annotation { "Feature Type Name" : "Feature", "Feature Type Description" : "" }
export const myFeature = defineFeature(function(context is Context, id is Id, definition is map)
    precondition{}
    {
        {
            assignVariable(context, id + "F0", {"name" : "SignDepth", "anyValue" : 1 / 8});
        }
        {
            var Q0;
            Q0=qCreatedBy(makeId("Front.planeOp"),FACE);
            var sketch = newSketch(context, id + "F1", { "sketchPlane" : qUnion([Q0])});
            skLineSegment(sketch, "E0.bottom", {"start": v(-106.06, 127) * mm, "end": v(0, 127) * mm});
            skLineSegment(sketch, "E0.top", {"start": v(-106.06, 0) * mm, "end": v(0, 0) * mm});
            skLineSegment(sketch, "E0.left", {"start": v(-106.06, 127) * mm, "end": v(-106.06, 0) * mm});
            skLineSegment(sketch, "E0.right", {"start": v(0, 127) * mm, "end": v(0, 0) * mm});
            skLineSegment(sketch, "E1.bottom", {"start": v(-105.6, 126.55) * mm, "end": v(-0.45, 126.55) * mm});
            skLineSegment(sketch, "E1.top", {"start": v(-105.6, 0.45) * mm, "end": v(-0.45, 0.45) * mm});
            skLineSegment(sketch, "E1.left", {"start": v(-105.6, 126.55) * mm, "end": v(-105.6, 0.45) * mm});
            skLineSegment(sketch, "E1.right", {"start": v(-0.45, 126.55) * mm, "end": v(-0.45, 0.45) * mm});
            skSolve(sketch);
        }
        {
            var Q0;
            Q0 = qSketchRegion(id + "F1", true);
            extrude(context, id + "F2", {"entities" : qUnion([Q0]), "depth" : (getVariable(context, 'SignDepth')) * mm, "offsetDistance" : 25.4 * mm});
        }
        {
            var Q0;
            Q0=qCreatedBy(makeId("Front.planeOp"),FACE);
            var sketch = newSketch(context, id + "F3", { "sketchPlane" : qUnion([Q0])});
            skLineSegment(sketch, "E2.bottom", {"start": v(-105.6, 126.55) * mm, "end": v(-0.45, 126.55) * mm});
            skLineSegment(sketch, "E2.top", {"start": v(-105.6, 0.45) * mm, "end": v(-0.45, 0.45) * mm});
            skLineSegment(sketch, "E2.left", {"start": v(-105.6, 126.55) * mm, "end": v(-105.6, 0.45) * mm});
            skLineSegment(sketch, "E2.right", {"start": v(-0.45, 126.55) * mm, "end": v(-0.45, 0.45) * mm});
            skSolve(sketch);
        }
        {
            var Q0;
            Q0 = qSketchRegion(id + "F3", true);
            extrude(context, id + "F4", {"entities" : qUnion([Q0]), "depth" : (getVariable(context, 'SignDepth')) * mm, "offsetDistance" : 25.4 * mm});
        }
        {
            var Q0;
            Q0=makeQuery(id+"F4.opExtrude","CAP_FACE",FACE,{"disambiguationData":[OSD([sQuery(id+"F3.wireOp",EDGE,"E2.bottom"),sQuery(id+"F3.wireOp",EDGE,"E2.top"),sQuery(id+"F3.wireOp",EDGE,"E2.left"),sQuery(id+"F3.wireOp",EDGE,"E2.right")])],"isStart":false});
            var sketch = newSketch(context, id + "F5", { "sketchPlane" : qUnion([Q0])});
            skText(sketch, "E3", { "text": "POLICE TELEPHONE", "fontName": "RobotoSlab-Regular.ttf"});
            skText(sketch, "E4", { "text": "FREE", "fontName": "NotoSerif-Bold.ttf"});
            skText(sketch, "E5", { "text": "FOR USE OF", "fontName": "NotoSerif-Regular.ttf"});
            skText(sketch, "E6", { "text": "PUBLIC", "fontName": "NotoSerif-Bold.ttf"});
            skText(sketch, "E7", { "text": "ADVICE & ASSISTANCE\n", "fontName": "NotoSans-Regular.ttf"});
            skText(sketch, "E8", { "text": "OBTAINABLE IMMEDIATELY", "fontName": "OpenSans-Regular.ttf"});
            skText(sketch, "E9", { "text": "OFFICER & CARS", "fontName": "OpenSans-Regular.ttf"});
            skText(sketch, "E10", { "text": "RESPOND TO ALL CALLS", "fontName": "OpenSans-Regular.ttf"});
            skText(sketch, "E11", { "text": "PULL TO OPEN", "fontName": "OpenSans-Regular.ttf"});
            const initialGuessF5  = {"E3": [-0.05014, 0.12437, 1, 0, 0.00018], "E4": [-0.05014, 0.12389, 1, 0, 0.00066], "E5": [-0.05014, 0.12424, 1, 0, 0.0003], "E6": [-0.05014, 0.12408, 1, 0, 0.00046], "E7": [-0.05014, 0.12438, 1, 0, 0.00017], "E8": [-0.07343, 0.0752, 1, 0, 0.00276], "E9": [-0.07343, 0.07332, 1, 0, 0.00465], "E10": [-0.07343, 0.07482, 1, 0, 0.00314], "E11": [-0.07343, 0.07283, 1, 0, 0.00513]};
            skSetInitialGuess(sketch, initialGuessF5);
            skSolve(sketch);
        }
        {
            var Q0;
            Q0 = qSketchRegion(id + "F5", true);
            extrude(context, id + "F6", {"entities" : qUnion([Q0]), "oppositeDirection" : true, "depth" : (getVariable(context, 'SignDepth') - (1 / 16)) * mm, "offsetDistance" : 25.4 * mm});
        }
        {
            var Q0;
            Q0=makeQuery(id+"F6.opExtrude","CAP_FACE",FACE,{"disambiguationData":[OSD([sQuery(id+"F5.wireOp",EDGE,"E4.sketch_text.stroke-32"),sQuery(id+"F5.wireOp",EDGE,"E4.sketch_text.stroke-33"),sQuery(id+"F5.wireOp",EDGE,"E4.sketch_text.stroke-34"),sQuery(id+"F5.wireOp",EDGE,"E4.sketch_text.stroke-35"),sQuery(id+"F5.wireOp",EDGE,"E4.sketch_text.stroke-36"),sQuery(id+"F5.wireOp",EDGE,"E4.sketch_text.stroke-37"),sQuery(id+"F5.wireOp",EDGE,"E4.sketch_text.stroke-38"),sQuery(id+"F5.wireOp",EDGE,"E4.sketch_text.stroke-39"),sQuery(id+"F5.wireOp",EDGE,"E4.sketch_text.stroke-40"),sQuery(id+"F5.wireOp",EDGE,"E4.sketch_text.stroke-41"),sQuery(id+"F5.wireOp",EDGE,"E4.sketch_text.stroke-42"),sQuery(id+"F5.wireOp",EDGE,"E4.sketch_text.stroke-43"),sQuery(id+"F5.wireOp",EDGE,"E4.sketch_text.stroke-44"),sQuery(id+"F5.wireOp",EDGE,"E4.sketch_text.stroke-45"),sQuery(id+"F5.wireOp",EDGE,"E4.sketch_text.stroke-46"),sQuery(id+"F5.wireOp",EDGE,"E4.sketch_text.stroke-47"),sQuery(id+"F5.wireOp",EDGE,"E4.sketch_text.stroke-48"),sQuery(id+"F5.wireOp",EDGE,"E4.sketch_text.stroke-49"),sQuery(id+"F5.wireOp",EDGE,"E4.sketch_text.stroke-50"),sQuery(id+"F5.wireOp",EDGE,"E4.sketch_text.stroke-51"),sQuery(id+"F5.wireOp",EDGE,"E4.sketch_text.stroke-52"),sQuery(id+"F5.wireOp",EDGE,"E4.sketch_text.stroke-53"),sQuery(id+"F5.wireOp",EDGE,"E4.sketch_text.stroke-54"),sQuery(id+"F5.wireOp",EDGE,"E4.sketch_text.stroke-55"),sQuery(id+"F5.wireOp",EDGE,"E4.sketch_text.stroke-56"),sQuery(id+"F5.wireOp",EDGE,"E4.sketch_text.stroke-57"),sQuery(id+"F5.wireOp",EDGE,"E4.sketch_text.stroke-58"),sQuery(id+"F5.wireOp",EDGE,"E4.sketch_text.stroke-59"),sQuery(id+"F5.wireOp",EDGE,"E4.sketch_text.stroke-60"),sQuery(id+"F5.wireOp",EDGE,"E4.sketch_text.stroke-61"),sQuery(id+"F5.wireOp",EDGE,"E4.sketch_text.stroke-62"),sQuery(id+"F5.wireOp",EDGE,"E4.sketch_text.stroke-63"),sQuery(id+"F5.wireOp",EDGE,"E4.sketch_text.stroke-64"),sQuery(id+"F5.wireOp",EDGE,"E4.sketch_text.stroke-65"),sQuery(id+"F5.wireOp",EDGE,"E4.sketch_text.stroke-66"),sQuery(id+"F5.wireOp",EDGE,"E4.sketch_text.stroke-67"),sQuery(id+"F5.wireOp",EDGE,"E4.sketch_text.stroke-68"),sQuery(id+"F5.wireOp",EDGE,"E4.sketch_text.stroke-69"),sQuery(id+"F5.wireOp",EDGE,"E4.sketch_text.stroke-70"),sQuery(id+"F5.wireOp",EDGE,"E4.sketch_text.stroke-71"),sQuery(id+"F5.wireOp",EDGE,"E4.sketch_text.stroke-72"),sQuery(id+"F5.wireOp",EDGE,"E4.sketch_text.stroke-73"),sQuery(id+"F5.wireOp",EDGE,"E4.sketch_text.stroke-74"),sQuery(id+"F5.wireOp",EDGE,"E4.sketch_text.stroke-75"),sQuery(id+"F5.wireOp",EDGE,"E4.sketch_text.stroke-76"),sQuery(id+"F5.wireOp",EDGE,"E4.sketch_text.stroke-77"),sQuery(id+"F5.wireOp",EDGE,"E4.sketch_text.stroke-78"),sQuery(id+"F5.wireOp",EDGE,"E4.sketch_text.stroke-79"),sQuery(id+"F5.wireOp",EDGE,"E4.sketch_text.stroke-80"),sQuery(id+"F5.wireOp",EDGE,"E4.sketch_text.stroke-81"),sQuery(id+"F5.wireOp",EDGE,"E4.sketch_text.stroke-82"),sQuery(id+"F5.wireOp",EDGE,"E4.sketch_text.stroke-83"),sQuery(id+"F5.wireOp",EDGE,"E4.sketch_text.stroke-84")])],"isStart":false});
            var sketch = newSketch(context, id + "F7", { "sketchPlane" : qUnion([Q0])});
            skLineSegment(sketch, "E12.bottom", {"start": v(8.45, 113.9) * mm, "end": v(98.1, 113.9) * mm});
            skLineSegment(sketch, "E12.top", {"start": v(8.45, 113.87) * mm, "end": v(53.25, 113.87) * mm});
            skLineSegment(sketch, "E12.left", {"start": v(8.45, 113.9) * mm, "end": v(8.45, 113.87) * mm});
            skLineSegment(sketch, "E12.right", {"start": v(98.1, 113.9) * mm, "end": v(98.1, 113.87) * mm});
            skLineSegment(sketch, "E13.bottom", {"start": v(38.19, 102.7) * mm, "end": v(53.25, 102.7) * mm});
            skLineSegment(sketch, "E13.top", {"start": v(38.19, 102.68) * mm, "end": v(53.25, 102.68) * mm});
            skLineSegment(sketch, "E13.left", {"start": v(38.19, 102.7) * mm, "end": v(38.19, 102.68) * mm});
            skLineSegment(sketch, "E13.right", {"start": v(68.48, 102.7) * mm, "end": v(68.48, 102.68) * mm});
            skLineSegment(sketch, "E14.bottom", {"start": v(27.21, 87.3) * mm, "end": v(53.25, 87.3) * mm});
            skLineSegment(sketch, "E14.top", {"start": v(27.21, 87.27) * mm, "end": v(53.25, 87.27) * mm});
            skLineSegment(sketch, "E14.left", {"start": v(27.21, 87.3) * mm, "end": v(27.21, 87.27) * mm});
            skLineSegment(sketch, "E14.right", {"start": v(78.88, 87.3) * mm, "end": v(78.88, 87.27) * mm});
            skLineSegment(sketch, "E15.bottom", {"start": v(33.5, 72.5) * mm, "end": v(53.25, 72.5) * mm});
            skLineSegment(sketch, "E15.top", {"start": v(33.5, 72.48) * mm, "end": v(49.48, 72.48) * mm});
            skLineSegment(sketch, "E15.left", {"start": v(33.5, 72.5) * mm, "end": v(33.5, 72.48) * mm});
            skLineSegment(sketch, "E15.right", {"start": v(77.3, 72.5) * mm, "end": v(77.3, 72.48) * mm});
            skLineSegment(sketch, "E16.bottom", {"start": v(16.99, 54.8) * mm, "end": v(49.48, 54.8) * mm});
            skLineSegment(sketch, "E16.top", {"start": v(16.99, 54.78) * mm, "end": v(49.48, 54.78) * mm});
            skLineSegment(sketch, "E16.left", {"start": v(16.99, 54.8) * mm, "end": v(16.99, 54.78) * mm});
            skLineSegment(sketch, "E16.right", {"start": v(88.68, 54.8) * mm, "end": v(88.68, 54.78) * mm});
            skLineSegment(sketch, "E17.bottom", {"start": v(10.24, 45.92) * mm, "end": v(49.48, 45.92) * mm});
            skLineSegment(sketch, "E17.top", {"start": v(10.24, 45.9) * mm, "end": v(49.48, 45.9) * mm});
            skLineSegment(sketch, "E17.left", {"start": v(10.24, 45.92) * mm, "end": v(10.24, 45.9) * mm});
            skLineSegment(sketch, "E17.right", {"start": v(97.52, 45.92) * mm, "end": v(97.52, 45.9) * mm});
            skLineSegment(sketch, "E18.bottom", {"start": v(29.77, 33.68) * mm, "end": v(49.48, 33.68) * mm});
            skLineSegment(sketch, "E18.top", {"start": v(29.77, 33.66) * mm, "end": v(49.48, 33.66) * mm});
            skLineSegment(sketch, "E18.left", {"start": v(29.77, 33.68) * mm, "end": v(29.77, 33.66) * mm});
            skLineSegment(sketch, "E18.right", {"start": v(76.3, 33.68) * mm, "end": v(76.3, 33.66) * mm});
            skLineSegment(sketch, "E19.bottom", {"start": v(19.2, 25.81) * mm, "end": v(49.48, 25.81) * mm});
            skLineSegment(sketch, "E19.top", {"start": v(19.2, 25.79) * mm, "end": v(49.48, 25.79) * mm});
            skLineSegment(sketch, "E19.left", {"start": v(19.2, 25.81) * mm, "end": v(19.2, 25.79) * mm});
            skLineSegment(sketch, "E19.right", {"start": v(86.92, 25.81) * mm, "end": v(86.92, 25.79) * mm});
            skLineSegment(sketch, "E20.bottom", {"start": v(10.07, 10.9) * mm, "end": v(49.48, 10.9) * mm});
            skLineSegment(sketch, "E20.top", {"start": v(10.07, 10.88) * mm, "end": v(95.56, 10.88) * mm});
            skLineSegment(sketch, "E20.left", {"start": v(10.07, 10.9) * mm, "end": v(10.07, 10.88) * mm});
            skLineSegment(sketch, "E20.right", {"start": v(95.56, 10.9) * mm, "end": v(95.56, 10.88) * mm});
            skLineSegment(sketch, "E21.left", {"start": v(49.48, 72.48) * mm, "end": v(49.48, 54.8) * mm});
            skLineSegment(sketch, "E21.right", {"start": v(49.5, 72.48) * mm, "end": v(49.5, 54.8) * mm});
            skLineSegment(sketch, "E22.trimOffspring", {"start": v(49.5, 72.48) * mm, "end": v(77.3, 72.48) * mm});
            skLineSegment(sketch, "E23.trimOffspring", {"start": v(49.5, 54.8) * mm, "end": v(88.68, 54.8) * mm});
            skLineSegment(sketch, "E24.trimOffspring", {"start": v(49.5, 54.78) * mm, "end": v(49.5, 45.92) * mm});
            skLineSegment(sketch, "E25.trimOffspring", {"start": v(49.48, 54.78) * mm, "end": v(49.48, 45.92) * mm});
            skLineSegment(sketch, "E26.trimOffspring", {"start": v(49.5, 54.78) * mm, "end": v(88.68, 54.78) * mm});
            skLineSegment(sketch, "E27.trimOffspring", {"start": v(49.5, 45.92) * mm, "end": v(97.52, 45.92) * mm});
            skLineSegment(sketch, "E28.trimOffspring", {"start": v(49.5, 45.9) * mm, "end": v(97.52, 45.9) * mm});
            skLineSegment(sketch, "E29.trimOffspring", {"start": v(49.5, 45.9) * mm, "end": v(49.5, 33.68) * mm});
            skLineSegment(sketch, "E30.trimOffspring", {"start": v(49.48, 45.9) * mm, "end": v(49.48, 33.68) * mm});
            skLineSegment(sketch, "E31.trimOffspring", {"start": v(49.5, 33.68) * mm, "end": v(76.3, 33.68) * mm});
            skLineSegment(sketch, "E32.trimOffspring", {"start": v(49.5, 33.66) * mm, "end": v(76.3, 33.66) * mm});
            skLineSegment(sketch, "E33.trimOffspring", {"start": v(49.48, 33.66) * mm, "end": v(49.48, 25.81) * mm});
            skLineSegment(sketch, "E34.trimOffspring", {"start": v(49.5, 33.66) * mm, "end": v(49.5, 25.81) * mm});
            skLineSegment(sketch, "E35.trimOffspring", {"start": v(49.5, 25.81) * mm, "end": v(86.92, 25.81) * mm});
            skLineSegment(sketch, "E36.trimOffspring", {"start": v(49.5, 25.79) * mm, "end": v(86.92, 25.79) * mm});
            skLineSegment(sketch, "E37.trimOffspring", {"start": v(49.48, 25.79) * mm, "end": v(49.48, 10.9) * mm});
            skLineSegment(sketch, "E38.trimOffspring", {"start": v(49.5, 25.79) * mm, "end": v(49.5, 10.9) * mm});
            skLineSegment(sketch, "E39.trimOffspring", {"start": v(49.5, 10.9) * mm, "end": v(95.56, 10.9) * mm});
            skLineSegment(sketch, "E40.left", {"start": v(53.25, 72.5) * mm, "end": v(53.25, 87.27) * mm});
            skLineSegment(sketch, "E40.right", {"start": v(53.27, 72.5) * mm, "end": v(53.27, 87.27) * mm});
            skLineSegment(sketch, "E41.trimOffspring", {"start": v(53.27, 72.5) * mm, "end": v(77.3, 72.5) * mm});
            skLineSegment(sketch, "E42.trimOffspring", {"start": v(53.27, 87.3) * mm, "end": v(78.88, 87.3) * mm});
            skLineSegment(sketch, "E43.trimOffspring", {"start": v(53.27, 87.27) * mm, "end": v(78.88, 87.27) * mm});
            skLineSegment(sketch, "E44.trimOffspring", {"start": v(53.27, 87.3) * mm, "end": v(53.27, 102.68) * mm});
            skLineSegment(sketch, "E45.trimOffspring", {"start": v(53.25, 87.3) * mm, "end": v(53.25, 102.68) * mm});
            skLineSegment(sketch, "E46.trimOffspring", {"start": v(53.27, 102.7) * mm, "end": v(53.27, 113.87) * mm});
            skLineSegment(sketch, "E47.trimOffspring", {"start": v(53.27, 102.7) * mm, "end": v(68.48, 102.7) * mm});
            skLineSegment(sketch, "E48.trimOffspring", {"start": v(53.25, 102.7) * mm, "end": v(53.25, 113.87) * mm});
            skLineSegment(sketch, "E49.trimOffspring", {"start": v(53.27, 102.68) * mm, "end": v(68.48, 102.68) * mm});
            skLineSegment(sketch, "E50.trimOffspring", {"start": v(53.27, 113.87) * mm, "end": v(98.1, 113.87) * mm});
            skPoint(sketch, "E40.top.end.orphan", {"position": v(53.27, 113.9) * mm});
            skLineSegment(sketch, "E51.bottom", {"start": v(62.47, 102.68) * mm, "end": v(62.5, 102.68) * mm});
            skLineSegment(sketch, "E51.top", {"start": v(62.47, 126.76) * mm, "end": v(62.5, 126.76) * mm});
            skLineSegment(sketch, "E51.left", {"start": v(62.47, 102.68) * mm, "end": v(62.47, 126.76) * mm});
            skLineSegment(sketch, "E51.right", {"start": v(62.5, 102.68) * mm, "end": v(62.5, 126.76) * mm});
            skSolve(sketch);
        }
        {
            var Q0;
            {var subQ0=sQuery(id+"F7.wireOp",EDGE,"E51.left");var subQ1=sQuery(id+"F7.wireOp",EDGE,"E47.trimOffspring");var subQ2=makeQuery(id+"F7.imprint","INTERSECT",VERTEX,{"derivedFrom":[subQ1,subQ0]});var subQ3=sQuery(id+"F7.wireOp",EDGE,"E51.right");var subQ5=makeQuery(id+"F7.imprint","IMPRINT",EDGE,{"disambiguationData":[TD([[subQ2,-1.0]])],"derivedFrom":subQ1});var subQ10=sQuery(id+"F7.wireOp",EDGE,"E44.trimOffspring");var subQ11=makeQuery(id+"F6.opExtrude","CAP_EDGE",EDGE,{"disambiguationData":[OSD([sQuery(id+"F5.wireOp",EDGE,"E4.sketch_text.stroke-58")])],"isStart":false});var subQ12=makeQuery(id+"F7.imprint","INTERSECT",VERTEX,{"derivedFrom":[subQ11,subQ10]});var subQ25=makeQuery(id+"F6.opExtrude","CAP_EDGE",EDGE,{"disambiguationData":[OSD([sQuery(id+"F5.wireOp",EDGE,"E4.sketch_text.stroke-63")])],"isStart":false});var subQ26=makeQuery(id+"F7.imprint","INTERSECT",VERTEX,{"derivedFrom":[subQ25,subQ1]});var subQ27=makeQuery(id+"F6.opExtrude","CAP_EDGE",EDGE,{"disambiguationData":[OSD([sQuery(id+"F5.wireOp",EDGE,"E4.sketch_text.stroke-65")])],"isStart":false});var subQ28=makeQuery(id+"F7.imprint","INTERSECT",VERTEX,{"derivedFrom":[subQ27,subQ1]});var subQ33=makeQuery(id+"F6.opExtrude","CAP_EDGE",EDGE,{"disambiguationData":[OSD([sQuery(id+"F5.wireOp",EDGE,"E4.sketch_text.stroke-51")])],"isStart":false});var subQ34=makeQuery(id+"F7.imprint","INTERSECT",VERTEX,{"derivedFrom":[subQ33,subQ1]});var subQ37=sQuery(id+"F7.wireOp",EDGE,"E13.right");var subQ42=sQuery(id+"F7.wireOp",EDGE,"E12.bottom");var subQ43=makeQuery(id+"F7.imprint","INTERSECT",VERTEX,{"derivedFrom":[subQ42,subQ3]});var subQ45=makeQuery(id+"F7.imprint","IMPRINT",EDGE,{"disambiguationData":[TD([[subQ43,1.0]])],"derivedFrom":subQ42});var subQ46=sQuery(id+"F7.wireOp",EDGE,"E51.top");var subQ47=sQuery(id+"F7.wireOp",EDGE,"E14.bottom");var subQ54=sQuery(id+"F7.wireOp",EDGE,"E12.right");Q0=qUnion([makeQuery(id+"F7.imprint","IMPRINT",FACE,{"disambiguationData":[TD([[subQ45,-1.0]])]}),makeQuery(id+"F7.imprint","IMPRINT",FACE,{"disambiguationData":[TD([[makeQuery(id+"F7.imprint","IMPRINT",EDGE,{"derivedFrom":subQ54}),-1.0]])]}),makeQuery(id+"F7.imprint","IMPRINT",FACE,{"disambiguationData":[TD([[makeQuery(id+"F7.imprint","IMPRINT",EDGE,{"derivedFrom":sQuery(id+"F7.wireOp",EDGE,"E12.top")}),1.0]])]}),makeQuery(id+"F7.imprint","IMPRINT",FACE,{"disambiguationData":[TD([[makeQuery(id+"F7.imprint","IMPRINT",EDGE,{"derivedFrom":subQ47}),-1.0]])]}),makeQuery(id+"F7.imprint","IMPRINT",FACE,{"disambiguationData":[TD([[makeQuery(id+"F7.imprint","IMPRINT",EDGE,{"derivedFrom":subQ46}),-1.0]])]}),makeQuery(id+"F7.imprint","IMPRINT",FACE,{"disambiguationData":[TD([[makeQuery(id+"F7.imprint","IMPRINT",EDGE,{"disambiguationData":[TD([[subQ28,-1.0]])],"derivedFrom":subQ1}),-1.0]])]}),makeQuery(id+"F7.imprint","IMPRINT",FACE,{"disambiguationData":[TD([[makeQuery(id+"F7.imprint","IMPRINT",EDGE,{"disambiguationData":[TD([[subQ2,1.0]])],"derivedFrom":subQ1}),-1.0]])]}),makeQuery(id+"F7.imprint","IMPRINT",FACE,{"disambiguationData":[TD([[makeQuery(id+"F7.imprint","IMPRINT",EDGE,{"derivedFrom":subQ37}),-1.0]])]}),makeQuery(id+"F7.imprint","IMPRINT",FACE,{"disambiguationData":[TD([[makeQuery(id+"F7.imprint","IMPRINT",EDGE,{"disambiguationData":[TD([[subQ34,-1.0]])],"derivedFrom":subQ1}),-1.0]])]}),makeQuery(id+"F7.imprint","IMPRINT",FACE,{"disambiguationData":[TD([[makeQuery(id+"F7.imprint","IMPRINT",EDGE,{"disambiguationData":[TD([[subQ26,-1.0]])],"derivedFrom":subQ1}),-1.0]])]}),makeQuery(id+"F7.imprint","IMPRINT",FACE,{"disambiguationData":[TD([[subQ5,-1.0]])]}),makeQuery(id+"F7.imprint","IMPRINT",FACE,{"disambiguationData":[TD([[makeQuery(id+"F7.imprint","IMPRINT",EDGE,{"disambiguationData":[TD([[subQ12,-1.0]])],"derivedFrom":subQ10}),1.0]])]}),makeQuery(id+"F7.imprint","IMPRINT",FACE,{"disambiguationData":[TD([[subQ5,1.0]])]})]);}
            extrude(context, id + "F8", {"entities" : qUnion([Q0]), "depth" : 0.8 * mm, "offsetDistance" : 25.4 * mm});
        }
        {
            var Q0;
            Q0=makeQuery(id+"F6.opExtrude","SWEPT_BODY",BODY,{"disambiguationData":[OSD([sQuery(id+"F5.wireOp",EDGE,"E3.sketch_text.stroke-0"),sQuery(id+"F5.wireOp",EDGE,"E3.sketch_text.stroke-1"),sQuery(id+"F5.wireOp",EDGE,"E3.sketch_text.stroke-2"),sQuery(id+"F5.wireOp",EDGE,"E3.sketch_text.stroke-3"),sQuery(id+"F5.wireOp",EDGE,"E3.sketch_text.stroke-4"),sQuery(id+"F5.wireOp",EDGE,"E3.sketch_text.stroke-5"),sQuery(id+"F5.wireOp",EDGE,"E3.sketch_text.stroke-6"),sQuery(id+"F5.wireOp",EDGE,"E3.sketch_text.stroke-7"),sQuery(id+"F5.wireOp",EDGE,"E3.sketch_text.stroke-8"),sQuery(id+"F5.wireOp",EDGE,"E3.sketch_text.stroke-9"),sQuery(id+"F5.wireOp",EDGE,"E3.sketch_text.stroke-10"),sQuery(id+"F5.wireOp",EDGE,"E3.sketch_text.stroke-11"),sQuery(id+"F5.wireOp",EDGE,"E3.sketch_text.stroke-12"),sQuery(id+"F5.wireOp",EDGE,"E3.sketch_text.stroke-13"),sQuery(id+"F5.wireOp",EDGE,"E3.sketch_text.stroke-14"),sQuery(id+"F5.wireOp",EDGE,"E3.sketch_text.stroke-15"),sQuery(id+"F5.wireOp",EDGE,"E3.sketch_text.stroke-16"),sQuery(id+"F5.wireOp",EDGE,"E3.sketch_text.stroke-17"),sQuery(id+"F5.wireOp",EDGE,"E3.sketch_text.stroke-18"),sQuery(id+"F5.wireOp",EDGE,"E3.sketch_text.stroke-19"),sQuery(id+"F5.wireOp",EDGE,"E3.sketch_text.stroke-20"),sQuery(id+"F5.wireOp",EDGE,"E3.sketch_text.stroke-21"),sQuery(id+"F5.wireOp",EDGE,"E3.sketch_text.stroke-22")])]});
            var Q1;
            Q1=makeQuery(id+"F4.opExtrude","SWEPT_BODY",BODY,{"disambiguationData":[OSD([sQuery(id+"F3.wireOp",EDGE,"E2.bottom"),sQuery(id+"F3.wireOp",EDGE,"E2.top"),sQuery(id+"F3.wireOp",EDGE,"E2.left"),sQuery(id+"F3.wireOp",EDGE,"E2.right")])]});
            booleanBodies(context, id + "F9", {"operationType" : BooleanOperationType.SUBTRACTION, "tools" : qUnion([Q0]), "targets" : qUnion([Q1]), "keepTools" : true});
        }
    });